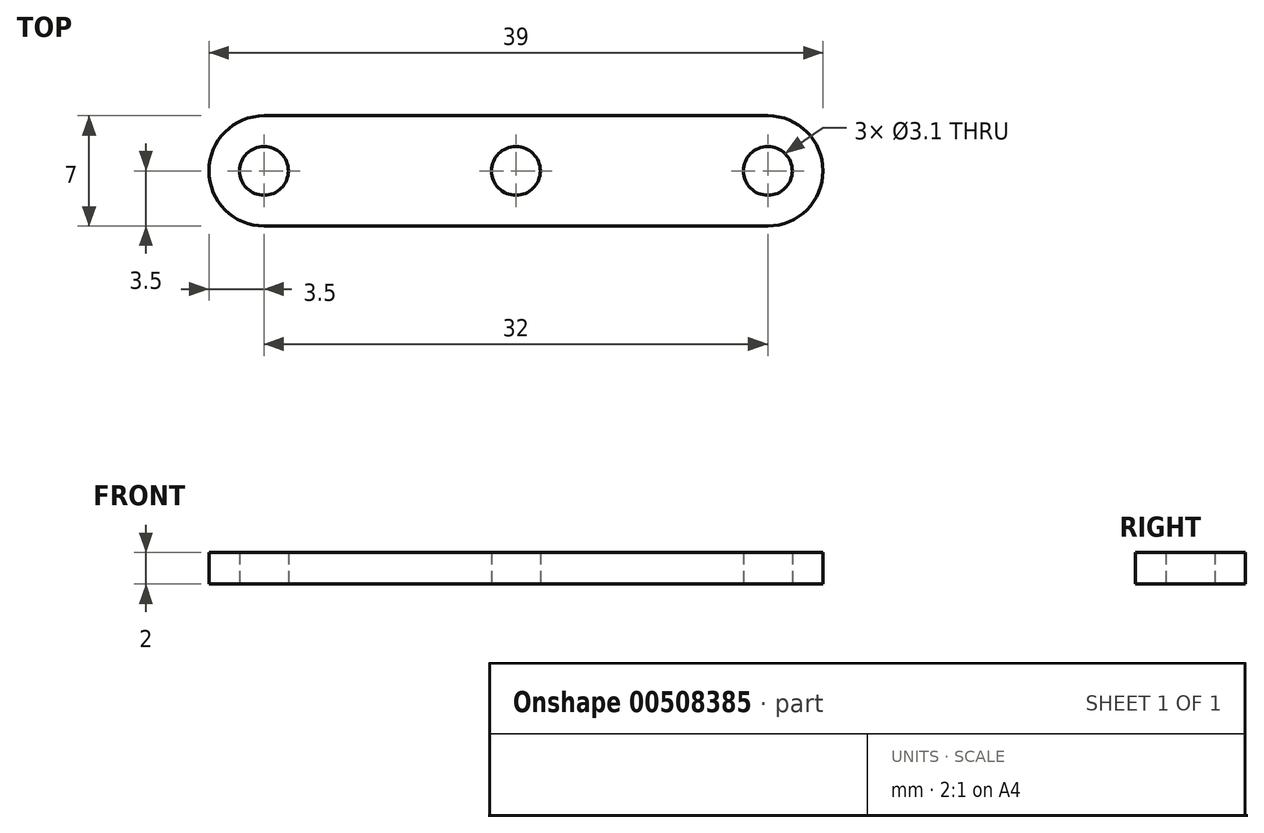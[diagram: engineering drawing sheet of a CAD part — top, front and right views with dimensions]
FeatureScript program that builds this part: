
annotation { "Feature Type Name" : "Feature", "Feature Type Description" : "" }
export const myFeature = defineFeature(function(context is Context, id is Id, definition is map)
    precondition{}
    {
        {
            var Q0;
            Q0=qCreatedBy(makeId("Top.planeOp"),FACE);
            var sketch = newSketch(context, id + "F0", { "sketchPlane" : qUnion([Q0])});
            skPoint(sketch, "E0.middle", {"position": v(0, 0) * mm});
            skCircle(sketch, "E1", {"center": v(0, 0) * mm, "radius": 1.55 * mm});
            skCircle(sketch, "E2", {"center": v(16, 0) * mm, "radius": 1.55 * mm});
            skCircle(sketch, "E3.MirrorC", {"center": v(-16, 0) * mm, "radius": 1.55 * mm});
            skLineSegment(sketch, "E4.bottom", {"start": v(16, -3.5) * mm, "end": v(-16, -3.5) * mm});
            skLineSegment(sketch, "E4.top", {"start": v(16, 3.5) * mm, "end": v(-16, 3.5) * mm});
            skLineSegment(sketch, "E4.left", {"start": v(19.5, 0) * mm, "end": v(19.5, 0) * mm});
            skLineSegment(sketch, "E4.right", {"start": v(-19.5, 0) * mm, "end": v(-19.5, 0) * mm});
            skPoint(sketch, "E5.visualSharp", {"position": v(-19.5, 3.5) * mm});
            skArc(sketch, "E5.filletArc", {"start": v(-16, 3.5) * mm, "mid": v(-18.47, 2.47) * mm, "end": v(-19.5, 0) * mm});
            skPoint(sketch, "E6.visualSharp", {"position": v(-19.5, -3.5) * mm});
            skArc(sketch, "E6.filletArc", {"start": v(-19.5, 0) * mm, "mid": v(-18.47, -2.47) * mm, "end": v(-16, -3.5) * mm});
            skPoint(sketch, "E7.visualSharp", {"position": v(19.5, 3.5) * mm});
            skArc(sketch, "E7.filletArc", {"start": v(19.5, 0) * mm, "mid": v(18.47, 2.47) * mm, "end": v(16, 3.5) * mm});
            skPoint(sketch, "E8.visualSharp", {"position": v(19.5, -3.5) * mm});
            skArc(sketch, "E8.filletArc", {"start": v(16, -3.5) * mm, "mid": v(18.47, -2.47) * mm, "end": v(19.5, 0) * mm});
            skSolve(sketch);
        }
        {
            var Q0;
            Q0 = qSketchRegion(id + "F0", true);
            extrude(context, id + "F1", {"entities" : qUnion([Q0]), "depth" : 2 * mm});
        }
    });
